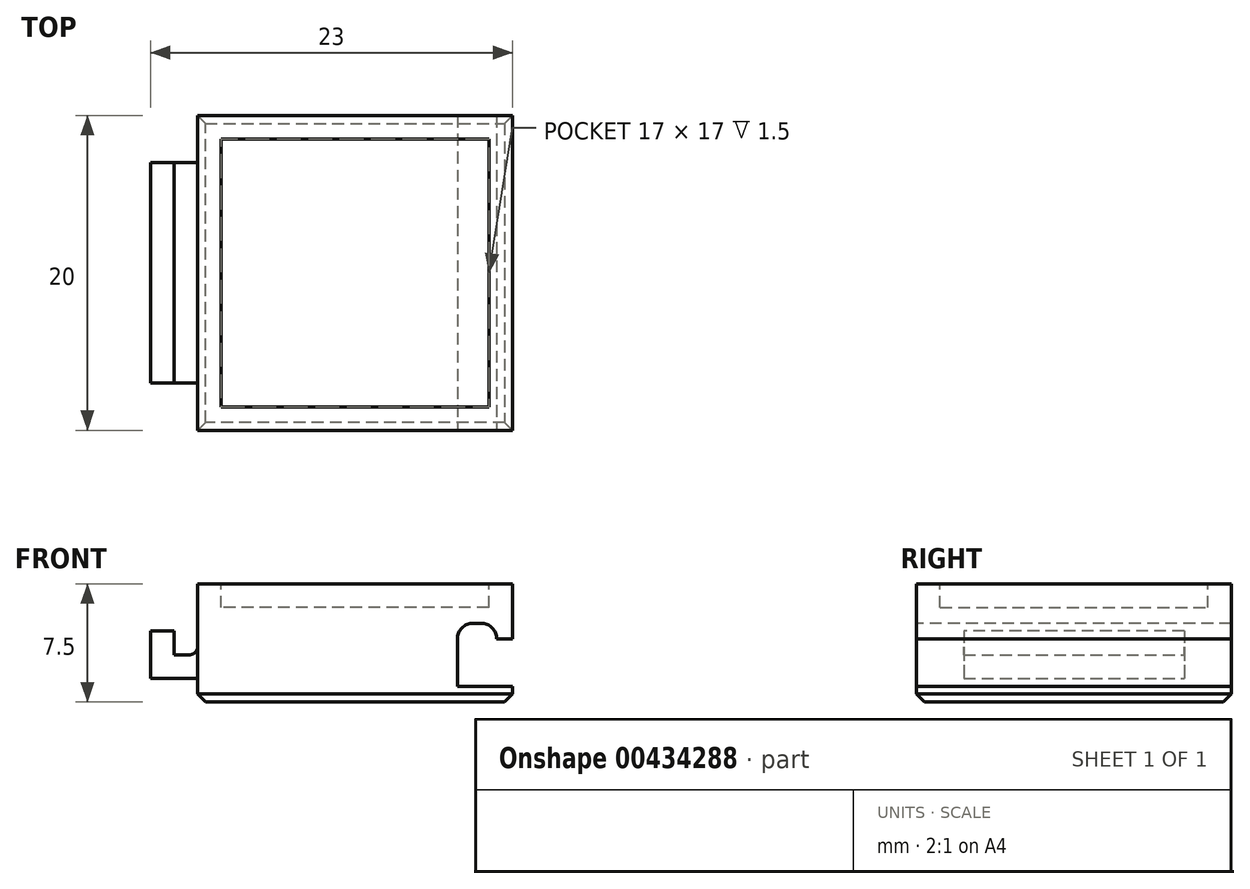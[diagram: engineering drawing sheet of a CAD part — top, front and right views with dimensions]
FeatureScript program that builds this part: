
annotation { "Feature Type Name" : "Feature", "Feature Type Description" : "" }
export const myFeature = defineFeature(function(context is Context, id is Id, definition is map)
    precondition{}
    {
        {
            var Q0;
            Q0=qCreatedBy(makeId("Top.planeOp"),FACE);
            var sketch = newSketch(context, id + "F0", { "sketchPlane" : qUnion([Q0])});
            skLineSegment(sketch, "E0.bottom", {"start": v(10, -10) * mm, "end": v(-10, -10) * mm});
            skLineSegment(sketch, "E0.top", {"start": v(10, 10) * mm, "end": v(-10, 10) * mm});
            skLineSegment(sketch, "E0.left", {"start": v(10, -10) * mm, "end": v(10, 10) * mm});
            skLineSegment(sketch, "E0.right", {"start": v(-10, -10) * mm, "end": v(-10, 10) * mm});
            skPoint(sketch, "E0.middle", {"position": v(0, 0) * mm});
            skSolve(sketch);
        }
        {
            var Q0;
            Q0 = qSketchRegion(id + "F0", true);
            extrude(context, id + "F1", {"entities" : qUnion([Q0]), "depth" : 1.5 * mm});
        }
        {
            var Q0;
            Q0=makeQuery(id+"F1.opExtrude","CAP_FACE",FACE,{"disambiguationData":[OSD([sQuery(id+"F0.wireOp",EDGE,"E0.bottom"),sQuery(id+"F0.wireOp",EDGE,"E0.top"),sQuery(id+"F0.wireOp",EDGE,"E0.left"),sQuery(id+"F0.wireOp",EDGE,"E0.right"),sQuery(id+"F0.wireOp",EDGE,"HCJZcMsu-V6uh-HxbJ-47AN-r2cQh35PogQR.bottom"),sQuery(id+"F0.wireOp",EDGE,"HCJZcMsu-V6uh-HxbJ-47AN-r2cQh35PogQR.top"),sQuery(id+"F0.wireOp",EDGE,"xbIhRUAe-GN2k-dXa3-QSfz-gwDgKAr4JCda")])],"isStart":false});
            var sketch = newSketch(context, id + "F2", { "sketchPlane" : qUnion([Q0])});
            skLineSegment(sketch, "E1.bottom", {"start": v(-10, 7) * mm, "end": v(-13, 7) * mm});
            skLineSegment(sketch, "E1.top", {"start": v(-10, -7) * mm, "end": v(-13, -7) * mm});
            skLineSegment(sketch, "E1.left", {"start": v(-10, 7) * mm, "end": v(-10, -7) * mm});
            skLineSegment(sketch, "E1.right", {"start": v(-13, 7) * mm, "end": v(-13, -7) * mm});
            skSolve(sketch);
        }
        {
            var Q0;
            Q0=makeQuery(id+"F2.imprint","IMPRINT",FACE,{"disambiguationData":[TD([[makeQuery(id+"F2.imprint","IMPRINT",EDGE,{"derivedFrom":sQuery(id+"F2.wireOp",EDGE,"E1.bottom")}),1.0]])]});
            extrude(context, id + "F3", {"entities" : qUnion([Q0]), "depth" : 1.5 * mm});
        }
        {
            var Q0;
            Q0=makeQuery(id+"F3.opExtrude","CAP_FACE",FACE,{"disambiguationData":[OSD([sQuery(id+"F2.wireOp",EDGE,"E1.bottom"),sQuery(id+"F2.wireOp",EDGE,"E1.top"),sQuery(id+"F2.wireOp",EDGE,"E1.left"),sQuery(id+"F2.wireOp",EDGE,"E1.right")])],"isStart":false});
            var sketch = newSketch(context, id + "F4", { "sketchPlane" : qUnion([Q0])});
            skLineSegment(sketch, "E2", {"start": v(-11.5, 7) * mm, "end": v(-11.5, -7) * mm});
            skSolve(sketch);
        }
        {
            var Q0;
            {var subQ0=sQuery(id+"F4.wireOp",EDGE,"E2");Q0=makeQuery(id+"F4.imprint","IMPRINT",FACE,{"disambiguationData":[TD([[makeQuery(id+"F4.imprint","IMPRINT",EDGE,{"derivedFrom":subQ0}),-1.0]])]});}
            extrude(context, id + "F5", {"entities" : qUnion([Q0]), "operationType" : NewBodyOperationType.ADD, "depth" : 1.5 * mm});
        }
        {
            var Q0;
            Q0=makeQuery(id+"F1.opExtrude","CAP_FACE",FACE,{"disambiguationData":[OSD([sQuery(id+"F0.wireOp",EDGE,"E0.bottom"),sQuery(id+"F0.wireOp",EDGE,"E0.top"),sQuery(id+"F0.wireOp",EDGE,"E0.left"),sQuery(id+"F0.wireOp",EDGE,"E0.right")])],"isStart":false});
            extrude(context, id + "F6", {"entities" : qUnion([Q0]), "operationType" : NewBodyOperationType.ADD, "depth" : 6 * mm});
        }
        {
            var Q0;
            Q0=makeQuery(id+"F6.opExtrude","CAP_FACE",FACE,{"disambiguationData":[OSD([sQuery(id+"F0.wireOp",EDGE,"E0.bottom"),sQuery(id+"F0.wireOp",EDGE,"E0.top"),sQuery(id+"F0.wireOp",EDGE,"E0.left"),sQuery(id+"F0.wireOp",EDGE,"E0.right")])],"isStart":false});
            var sketch = newSketch(context, id + "F7", { "sketchPlane" : qUnion([Q0])});
            skLineSegment(sketch, "E3.bottom", {"start": v(8.5, -8.5) * mm, "end": v(-8.5, -8.5) * mm});
            skLineSegment(sketch, "E3.top", {"start": v(8.5, 8.5) * mm, "end": v(-8.5, 8.5) * mm});
            skLineSegment(sketch, "E3.left", {"start": v(8.5, -8.5) * mm, "end": v(8.5, 8.5) * mm});
            skLineSegment(sketch, "E3.right", {"start": v(-8.5, -8.5) * mm, "end": v(-8.5, 8.5) * mm});
            skPoint(sketch, "E3.middle", {"position": v(0, 0) * mm});
            skSolve(sketch);
        }
        {
            var Q0;
            Q0=makeQuery(id+"F7.imprint","IMPRINT",FACE,{"disambiguationData":[TD([[makeQuery(id+"F7.imprint","IMPRINT",EDGE,{"derivedFrom":sQuery(id+"F7.wireOp",EDGE,"E3.bottom")}),-1.0]])]});
            extrude(context, id + "F8", {"entities" : qUnion([Q0]), "operationType" : NewBodyOperationType.REMOVE, "oppositeDirection" : true, "depth" : 1.5 * mm});
        }
        {
            var Q0;
            {var subQ0=sQuery(id+"F0.wireOp",EDGE,"E0.bottom");Q0=makeQuery(id+"FyvZftckYwPIOyA_1.boolean.opBoolean","MERGE",FACE,{"derivedFrom":[makeQuery(id+"F8DhuhfjgwzCXIn_1.boolean.opBoolean","MERGE",FACE,{"derivedFrom":[makeQuery(id+"F6.boolean.opBoolean","MERGE",FACE,{"derivedFrom":[makeQuery(id+"F1.opExtrude","SWEPT_FACE",FACE,{"disambiguationData":[OSD([subQ0])]}),makeQuery(id+"F6.opExtrude","SWEPT_FACE",FACE,{"disambiguationData":[OSD([subQ0])]})]}),makeQuery(id+"F8DhuhfjgwzCXIn_1.opExtrude","SWEPT_FACE",FACE,{"disambiguationData":[OSD([subQ0])]})]}),makeQuery(id+"FyvZftckYwPIOyA_1.opExtrude","SWEPT_FACE",FACE,{"disambiguationData":[OSD([subQ0])]})]});}
            var sketch = newSketch(context, id + "F9", { "sketchPlane" : qUnion([Q0])});
            skLineSegment(sketch, "E4.bottom", {"start": v(10, 1) * mm, "end": v(6.5, 1) * mm});
            skLineSegment(sketch, "E4.top", {"start": v(10, 4) * mm, "end": v(6.5, 4) * mm});
            skLineSegment(sketch, "E4.left", {"start": v(10, 1) * mm, "end": v(10, 4) * mm});
            skLineSegment(sketch, "E4.right", {"start": v(6.5, 1) * mm, "end": v(6.5, 4) * mm});
            skLineSegment(sketch, "E5.bottom", {"start": v(6.5, 4) * mm, "end": v(9, 4) * mm});
            skLineSegment(sketch, "E5.top", {"start": v(6.5, 5) * mm, "end": v(9, 5) * mm});
            skLineSegment(sketch, "E5.left", {"start": v(6.5, 4) * mm, "end": v(6.5, 5) * mm});
            skLineSegment(sketch, "E5.right", {"start": v(9, 4) * mm, "end": v(9, 5) * mm});
            skSolve(sketch);
        }
        {
            var Q0;
            Q0 = qSketchRegion(id + "F9", true);
            extrude(context, id + "F10", {"entities" : qUnion([Q0]), "operationType" : NewBodyOperationType.REMOVE, "endBound" : BoundingType.UP_TO_NEXT, "oppositeDirection" : true, "depth" : 25 * mm});
        }
        {
            var Q0;
            Q0=makeQuery(id+"F10.boolean.opBoolean","COPY",EDGE,{"derivedFrom":makeQuery(id+"F10.opExtrude","SWEPT_EDGE",EDGE,{"disambiguationData":[OSD([sQuery(id+"F9.wireOp",EDGE,"E5.top"),sQuery(id+"F9.wireOp",EDGE,"E5.left")])]})});
            var Q1;
            Q1=makeQuery(id+"F10.boolean.opBoolean","COPY",EDGE,{"derivedFrom":makeQuery(id+"F10.opExtrude","SWEPT_EDGE",EDGE,{"disambiguationData":[OSD([sQuery(id+"F9.wireOp",EDGE,"E5.top"),sQuery(id+"F9.wireOp",EDGE,"E5.right")])]})});
            fillet(context, id + "F11", {"entities" : qUnion([Q0, Q1]), "radius" : 1 * mm, "tangentPropagation" : true, "allowEdgeOverflow" : false});
        }
        {
            var Q0;
            Q0=makeQuery(id+"F3.opExtrude","CAP_EDGE",EDGE,{"disambiguationData":[OSD([sQuery(id+"F2.wireOp",EDGE,"E1.left")])],"isStart":false});
            fillet(context, id + "F12", {"entities" : qUnion([Q0]), "radius" : 0.5 * mm, "tangentPropagation" : true, "allowEdgeOverflow" : false});
        }
        {
            var Q0;
            Q0=makeQuery(id+"F1.opExtrude","CAP_FACE",FACE,{"disambiguationData":[OSD([sQuery(id+"F0.wireOp",EDGE,"E0.bottom"),sQuery(id+"F0.wireOp",EDGE,"E0.top"),sQuery(id+"F0.wireOp",EDGE,"E0.left"),sQuery(id+"F0.wireOp",EDGE,"E0.right")])],"isStart":true});
            chamfer(context, id + "F13", {"entities" : qUnion([Q0]), "width" : 0.5 * mm, "tangentPropagation" : true});
        }
    });
